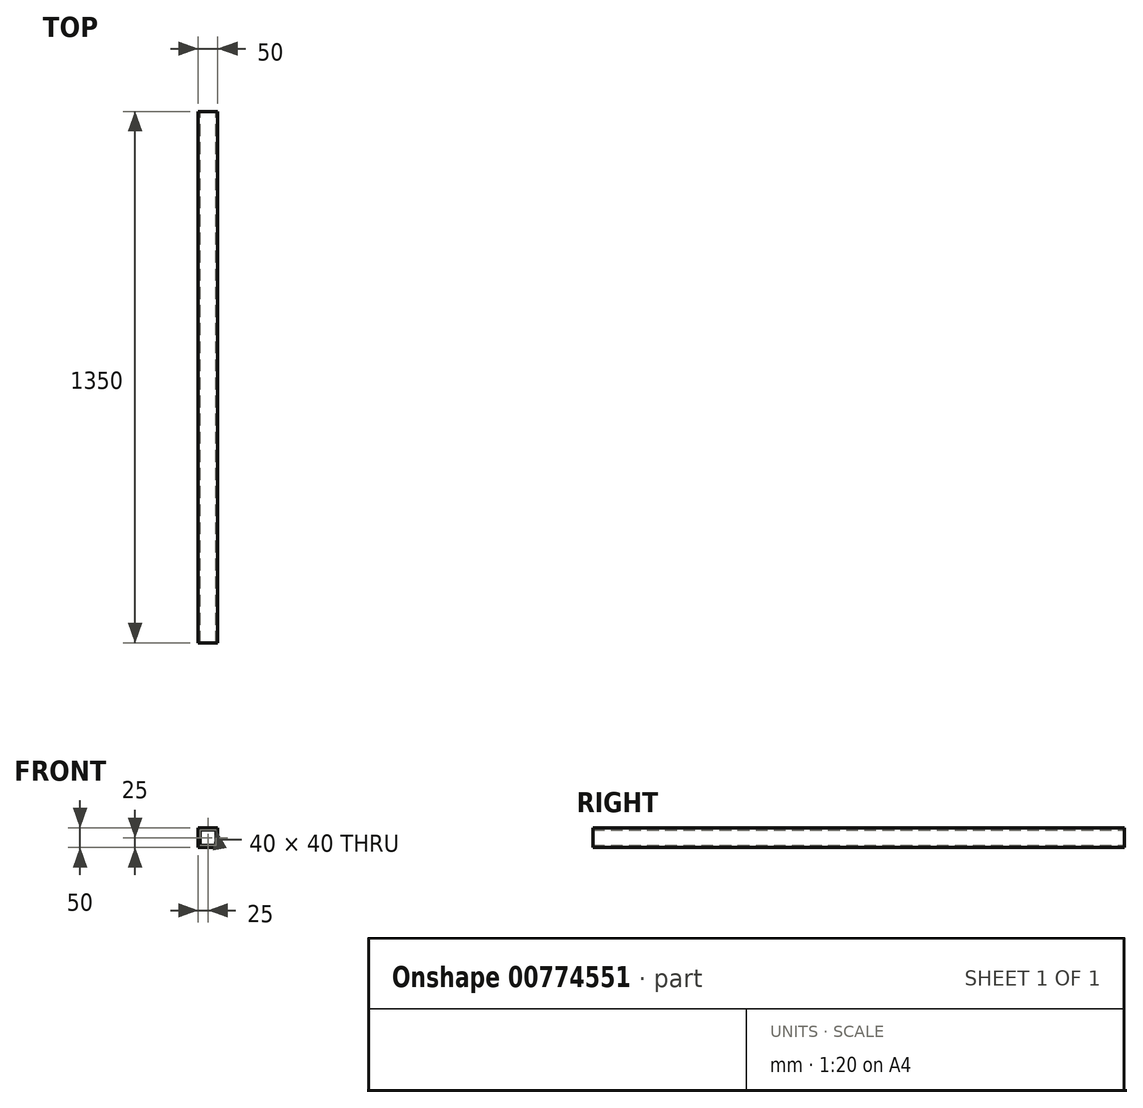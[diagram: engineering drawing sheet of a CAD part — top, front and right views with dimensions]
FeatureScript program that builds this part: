
annotation { "Feature Type Name" : "Feature", "Feature Type Description" : "" }
export const myFeature = defineFeature(function(context is Context, id is Id, definition is map)
    precondition{}
    {
        {
            var Q0;
            Q0=qCreatedBy(makeId("Front.planeOp"),FACE);
            var sketch = newSketch(context, id + "F0", { "sketchPlane" : qUnion([Q0])});
            skLineSegment(sketch, "E0.bottom", {"start": v(25, 25) * mm, "end": v(-25, 25) * mm});
            skLineSegment(sketch, "E0.top", {"start": v(25, -25) * mm, "end": v(-25, -25) * mm});
            skLineSegment(sketch, "E0.left", {"start": v(25, 25) * mm, "end": v(25, -25) * mm});
            skLineSegment(sketch, "E0.right", {"start": v(-25, 25) * mm, "end": v(-25, -25) * mm});
            skPoint(sketch, "E0.middle", {"position": v(0, 0) * mm});
            skLineSegment(sketch, "E1.bottom", {"start": v(20, -20) * mm, "end": v(-20, -20) * mm});
            skLineSegment(sketch, "E1.top", {"start": v(20, 20) * mm, "end": v(-20, 20) * mm});
            skLineSegment(sketch, "E1.left", {"start": v(20, -20) * mm, "end": v(20, 20) * mm});
            skLineSegment(sketch, "E1.right", {"start": v(-20, -20) * mm, "end": v(-20, 20) * mm});
            skSolve(sketch);
        }
        {
            var Q0;
            Q0 = qSketchRegion(id + "F0", true);
            extrude(context, id + "F1", {"entities" : qUnion([Q0]), "depth" : 1350 * mm, "offsetDistance" : 25 * mm});
        }
    });
